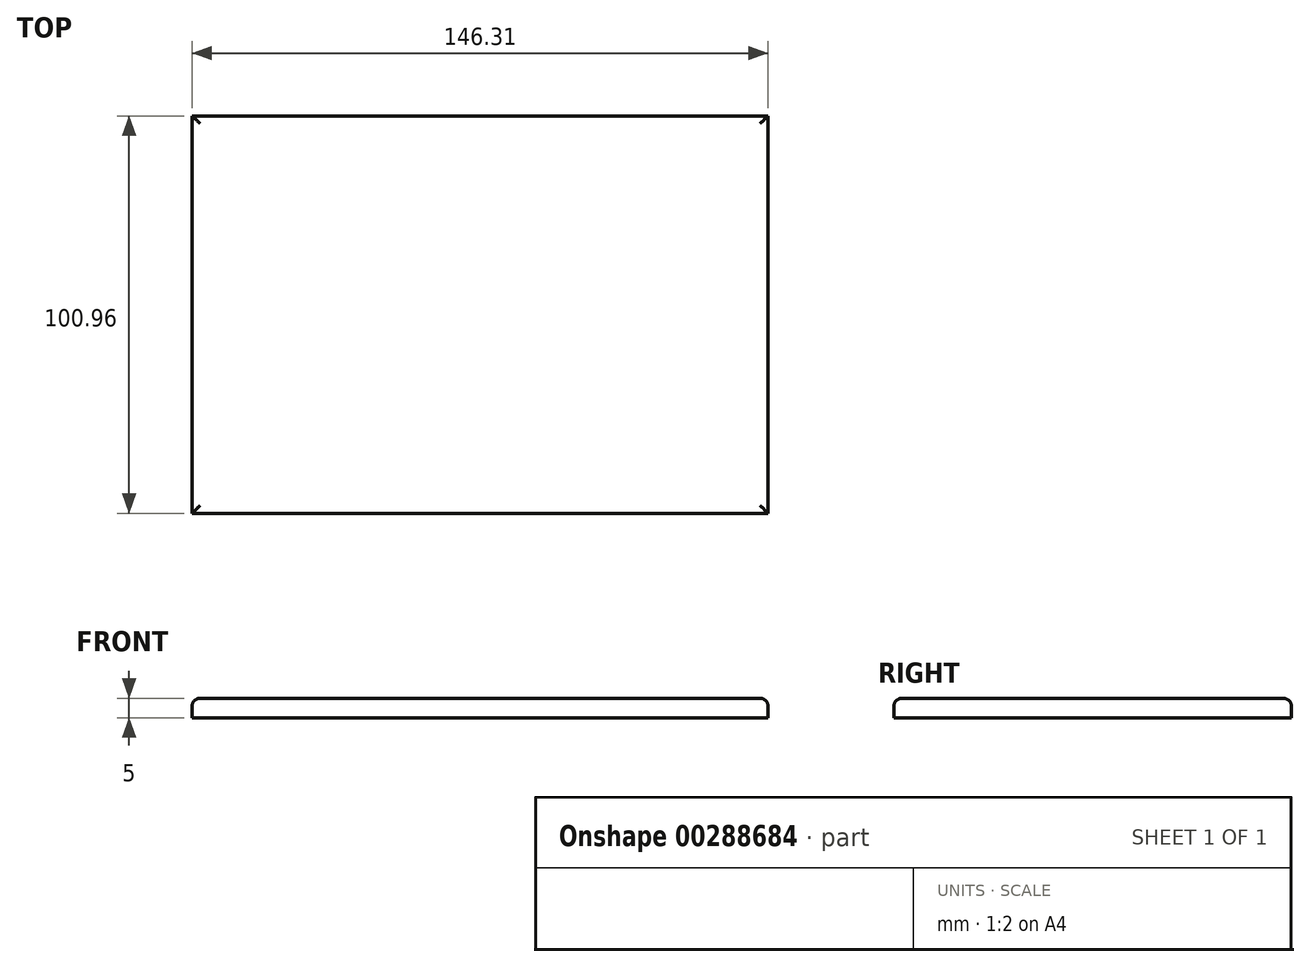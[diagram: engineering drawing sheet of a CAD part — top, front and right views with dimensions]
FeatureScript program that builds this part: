
annotation { "Feature Type Name" : "Feature", "Feature Type Description" : "" }
export const myFeature = defineFeature(function(context is Context, id is Id, definition is map)
    precondition{}
    {
        {
            var Q0;
            Q0=qCreatedBy(makeId("Top.planeOp"),FACE);
            var sketch = newSketch(context, id + "F0", { "sketchPlane" : qUnion([Q0])});
            skLineSegment(sketch, "E0.bottom", {"start": v(-88.27, 40.12) * mm, "end": v(58.04, 40.12) * mm});
            skLineSegment(sketch, "E0.top", {"start": v(-88.27, -60.84) * mm, "end": v(58.04, -60.84) * mm});
            skLineSegment(sketch, "E0.left", {"start": v(-88.27, 40.12) * mm, "end": v(-88.27, -60.84) * mm});
            skLineSegment(sketch, "E0.right", {"start": v(58.04, 40.12) * mm, "end": v(58.04, -60.84) * mm});
            skSolve(sketch);
        }
        {
            var Q0;
            Q0 = qSketchRegion(id + "F0", true);
            extrude(context, id + "F1", {"entities" : qUnion([Q0]), "depth" : 5 * mm});
        }
        {
            var Q0;
            Q0=makeQuery(id+"F1.opExtrude","CAP_EDGE",EDGE,{"disambiguationData":[OSD([sQuery(id+"F0.wireOp",EDGE,"E0.right")])],"isStart":false});
            var Q1;
            Q1=makeQuery(id+"F1.opExtrude","CAP_EDGE",EDGE,{"disambiguationData":[OSD([sQuery(id+"F0.wireOp",EDGE,"E0.bottom")])],"isStart":false});
            var Q2;
            Q2=makeQuery(id+"F1.opExtrude","CAP_EDGE",EDGE,{"disambiguationData":[OSD([sQuery(id+"F0.wireOp",EDGE,"E0.top")])],"isStart":false});
            var Q3;
            Q3=makeQuery(id+"F1.opExtrude","CAP_EDGE",EDGE,{"disambiguationData":[OSD([sQuery(id+"F0.wireOp",EDGE,"E0.left")])],"isStart":false});
            fillet(context, id + "F2", {"entities" : qUnion([Q0, Q1, Q2, Q3]), "radius" : 2 * mm, "tangentPropagation" : true, "allowEdgeOverflow" : false});
        }
    });
